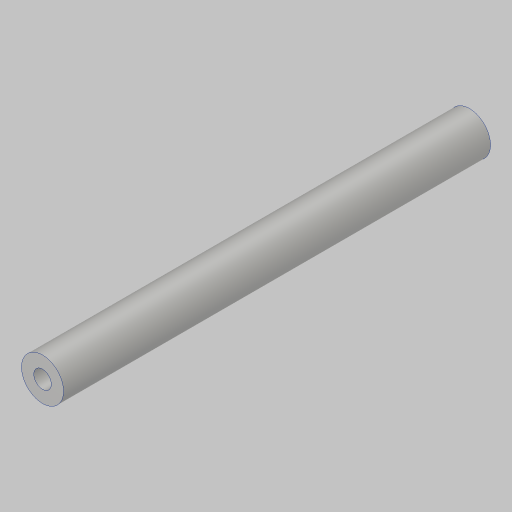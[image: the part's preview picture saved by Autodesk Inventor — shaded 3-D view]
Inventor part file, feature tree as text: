
AUTODESK INVENTOR PART (.ipt)
format: ipt  version: 2023.5 (Build 275446000, 446)  size: 107,008 bytes
history: native  units: in
note: dims shown in document units (in); Inventor stores cm internally (conversion verified against a paired STEP export)
features: extrude x1, hole x1
ambient origin geometry x8: Origin, YZ Plane, XZ Plane, XY Plane, X Axis, Y Axis, Z Axis, Center Point
bodies: Solid1 (feature_tree)
feature tree (2):
  extrude  "Extrusion1"  Depth=3.812in
  hole  "Hole1"  [1 undecoded]
note: 1 required parameter value undecoded (feature->parameter linkage not recoverable at this tier; creation-order binding heuristic only, values carry confidence <= 0.55)
